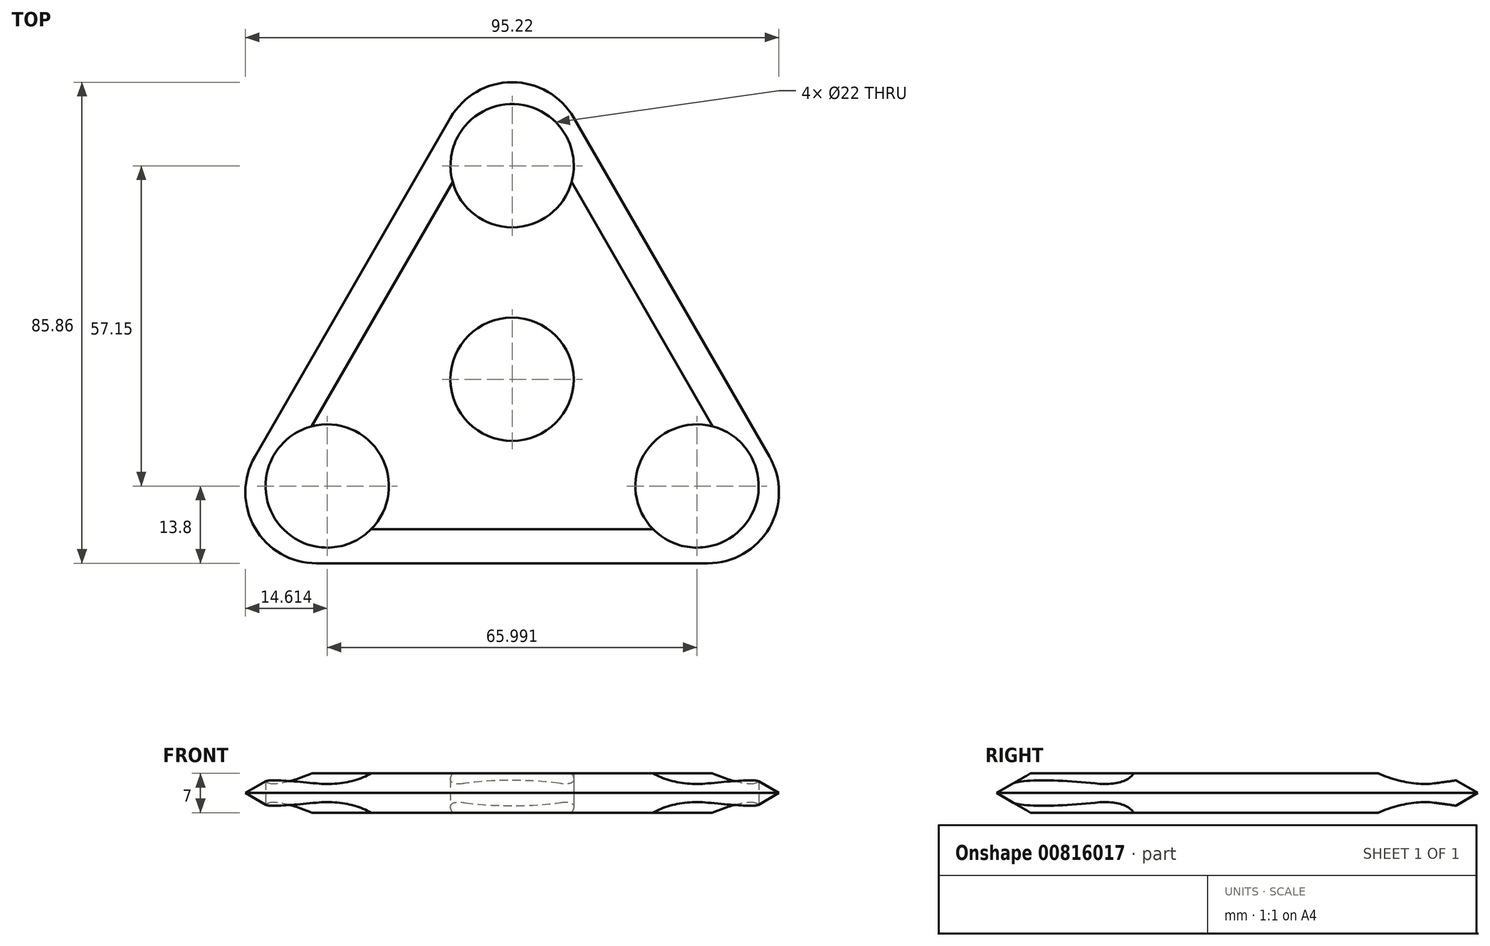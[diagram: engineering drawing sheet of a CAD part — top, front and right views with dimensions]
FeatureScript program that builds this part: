
annotation { "Feature Type Name" : "Feature", "Feature Type Description" : "" }
export const myFeature = defineFeature(function(context is Context, id is Id, definition is map)
    precondition{}
    {
        {
            var Q0;
            Q0=qCreatedBy(makeId("Top.planeOp"),FACE);
            var sketch = newSketch(context, id + "F0", { "sketchPlane" : qUnion([Q0])});
            skCircle(sketch, "E0", {"center": v(0, 0) * mm, "radius": 11 * mm});
            skCircle(sketch, "E1.cCircle", {"center": v(0, 0) * mm, "radius": 19.05 * mm, "construction": true});
            skLineSegment(sketch, "E1.0", {"start": v(0, 38.1) * mm, "end": v(33, -19.05) * mm});
            skLineSegment(sketch, "E1.1", {"start": v(33, -19.05) * mm, "end": v(-33, -19.05) * mm});
            skLineSegment(sketch, "E1.2", {"start": v(-33, -19.05) * mm, "end": v(0, 38.1) * mm});
            skPoint(sketch, "E1.0.midPoint", {"position": v(16.5, 9.53) * mm});
            skCircle(sketch, "E2", {"center": v(0, 38.1) * mm, "radius": 11 * mm});
            skCircle(sketch, "E3.1.0", {"center": v(-33, -19.05) * mm, "radius": 11 * mm});
            skCircle(sketch, "E3.2.0", {"center": v(33, -19.05) * mm, "radius": 11 * mm});
            skLineSegment(sketch, "E4.0", {"start": v(11, 46.66) * mm, "end": v(45.9, -13.8) * mm});
            skLineSegment(sketch, "E4.1", {"start": v(-45.9, -13.8) * mm, "end": v(-11, 46.66) * mm});
            skLineSegment(sketch, "E4.2", {"start": v(34.9, -32.85) * mm, "end": v(-34.9, -32.85) * mm});
            skPoint(sketch, "E5.visualSharp", {"position": v(0, 65.7) * mm});
            skArc(sketch, "E5.filletArc", {"start": v(11, 46.66) * mm, "mid": v(0, 53) * mm, "end": v(-11, 46.66) * mm});
            skPoint(sketch, "E6.visualSharp", {"position": v(-56.9, -32.85) * mm});
            skArc(sketch, "E6.filletArc", {"start": v(-45.9, -13.8) * mm, "mid": v(-45.9, -26.5) * mm, "end": v(-34.9, -32.85) * mm});
            skPoint(sketch, "E7.visualSharp", {"position": v(56.9, -32.85) * mm});
            skArc(sketch, "E7.filletArc", {"start": v(34.9, -32.85) * mm, "mid": v(45.9, -26.5) * mm, "end": v(45.9, -13.8) * mm});
            skSolve(sketch);
        }
        {
            var Q0;
            Q0=makeQuery(id+"F0.imprint","IMPRINT",FACE,{"disambiguationData":[TD([[makeQuery(id+"F0.imprint","IMPRINT",EDGE,{"derivedFrom":sQuery(id+"F0.wireOp",EDGE,"E4.0")}),-1.0]])]});
            var Q1;
            {var subQ0=sQuery(id+"F0.wireOp",EDGE,"E1.2");var subQ1=sQuery(id+"F0.wireOp",EDGE,"E1.0");var subQ2=makeQuery(id+"F0.imprint","INTERSECT",VERTEX,{"derivedFrom":[subQ1,subQ0]});Q1=makeQuery(id+"F0.imprint","IMPRINT",FACE,{"disambiguationData":[TD([[makeQuery(id+"F0.imprint","IMPRINT",EDGE,{"disambiguationData":[TD([[subQ2,-1.0]])],"derivedFrom":subQ1}),1.0]])]});}
            var Q2;
            Q2=makeQuery(id+"F0.imprint","IMPRINT",FACE,{"disambiguationData":[TD([[makeQuery(id+"F0.imprint","IMPRINT",EDGE,{"derivedFrom":sQuery(id+"F0.wireOp",EDGE,"E0")}),-1.0]])]});
            var Q3;
            {var subQ0=sQuery(id+"F0.wireOp",EDGE,"E1.2");var subQ1=sQuery(id+"F0.wireOp",EDGE,"E1.0");var subQ2=makeQuery(id+"F0.imprint","INTERSECT",VERTEX,{"derivedFrom":[subQ1,subQ0]});Q3=makeQuery(id+"F0.imprint","IMPRINT",FACE,{"disambiguationData":[TD([[makeQuery(id+"F0.imprint","IMPRINT",EDGE,{"disambiguationData":[TD([[subQ2,-1.0]])],"derivedFrom":subQ1}),-1.0]])]});}
            var Q4;
            {var subQ0=sQuery(id+"F0.wireOp",EDGE,"E1.2");var subQ1=sQuery(id+"F0.wireOp",EDGE,"E1.1");var subQ2=makeQuery(id+"F0.imprint","INTERSECT",VERTEX,{"derivedFrom":[subQ1,subQ0]});Q4=makeQuery(id+"F0.imprint","IMPRINT",FACE,{"disambiguationData":[TD([[makeQuery(id+"F0.imprint","IMPRINT",EDGE,{"disambiguationData":[TD([[subQ2,1.0]])],"derivedFrom":subQ1}),1.0]])]});}
            var Q5;
            {var subQ0=sQuery(id+"F0.wireOp",EDGE,"E1.1");var subQ1=sQuery(id+"F0.wireOp",EDGE,"E1.0");var subQ2=makeQuery(id+"F0.imprint","INTERSECT",VERTEX,{"derivedFrom":[subQ1,subQ0]});Q5=makeQuery(id+"F0.imprint","IMPRINT",FACE,{"disambiguationData":[TD([[makeQuery(id+"F0.imprint","IMPRINT",EDGE,{"disambiguationData":[TD([[subQ2,1.0]])],"derivedFrom":subQ1}),1.0]])]});}
            var Q6;
            {var subQ0=sQuery(id+"F0.wireOp",EDGE,"E1.1");var subQ1=sQuery(id+"F0.wireOp",EDGE,"E1.0");var subQ2=makeQuery(id+"F0.imprint","INTERSECT",VERTEX,{"derivedFrom":[subQ1,subQ0]});Q6=makeQuery(id+"F0.imprint","IMPRINT",FACE,{"disambiguationData":[TD([[makeQuery(id+"F0.imprint","IMPRINT",EDGE,{"disambiguationData":[TD([[subQ2,1.0]])],"derivedFrom":subQ1}),-1.0]])]});}
            var Q7;
            {var subQ0=sQuery(id+"F0.wireOp",EDGE,"E1.2");var subQ1=sQuery(id+"F0.wireOp",EDGE,"E1.1");var subQ2=makeQuery(id+"F0.imprint","INTERSECT",VERTEX,{"derivedFrom":[subQ1,subQ0]});Q7=makeQuery(id+"F0.imprint","IMPRINT",FACE,{"disambiguationData":[TD([[makeQuery(id+"F0.imprint","IMPRINT",EDGE,{"disambiguationData":[TD([[subQ2,1.0]])],"derivedFrom":subQ1}),-1.0]])]});}
            var Q8;
            Q8=makeQuery(id+"F0.imprint","IMPRINT",FACE,{"disambiguationData":[TD([[makeQuery(id+"F0.imprint","IMPRINT",EDGE,{"derivedFrom":sQuery(id+"F0.wireOp",EDGE,"E0")}),1.0]])]});
            extrude(context, id + "F1", {"entities" : qUnion([Q0, Q1, Q2, Q3, Q4, Q5, Q6, Q7, Q8]), "endBound" : BoundingType.SYMMETRIC, "depth" : 7 * mm, "offsetDistance" : 25.4 * mm, "hasDraft" : true, "draftAngle" : 60 * degree, "draftPullDirection" : true});
        }
        {
            var Q0;
            {var subQ0=sQuery(id+"F0.wireOp",EDGE,"E1.2");var subQ1=sQuery(id+"F0.wireOp",EDGE,"E1.1");var subQ2=makeQuery(id+"F0.imprint","INTERSECT",VERTEX,{"derivedFrom":[subQ1,subQ0]});Q0=makeQuery(id+"F0.imprint","IMPRINT",FACE,{"disambiguationData":[TD([[makeQuery(id+"F0.imprint","IMPRINT",EDGE,{"disambiguationData":[TD([[subQ2,1.0]])],"derivedFrom":subQ1}),1.0]])]});}
            var Q1;
            {var subQ0=sQuery(id+"F0.wireOp",EDGE,"E1.2");var subQ1=sQuery(id+"F0.wireOp",EDGE,"E1.1");var subQ2=makeQuery(id+"F0.imprint","INTERSECT",VERTEX,{"derivedFrom":[subQ1,subQ0]});Q1=makeQuery(id+"F0.imprint","IMPRINT",FACE,{"disambiguationData":[TD([[makeQuery(id+"F0.imprint","IMPRINT",EDGE,{"disambiguationData":[TD([[subQ2,1.0]])],"derivedFrom":subQ1}),-1.0]])]});}
            var Q2;
            Q2=makeQuery(id+"F0.imprint","IMPRINT",FACE,{"disambiguationData":[TD([[makeQuery(id+"F0.imprint","IMPRINT",EDGE,{"derivedFrom":sQuery(id+"F0.wireOp",EDGE,"E0")}),1.0]])]});
            var Q3;
            {var subQ0=sQuery(id+"F0.wireOp",EDGE,"E1.2");var subQ1=sQuery(id+"F0.wireOp",EDGE,"E1.0");var subQ2=makeQuery(id+"F0.imprint","INTERSECT",VERTEX,{"derivedFrom":[subQ1,subQ0]});Q3=makeQuery(id+"F0.imprint","IMPRINT",FACE,{"disambiguationData":[TD([[makeQuery(id+"F0.imprint","IMPRINT",EDGE,{"disambiguationData":[TD([[subQ2,-1.0]])],"derivedFrom":subQ1}),1.0]])]});}
            var Q4;
            {var subQ0=sQuery(id+"F0.wireOp",EDGE,"E1.2");var subQ1=sQuery(id+"F0.wireOp",EDGE,"E1.0");var subQ2=makeQuery(id+"F0.imprint","INTERSECT",VERTEX,{"derivedFrom":[subQ1,subQ0]});Q4=makeQuery(id+"F0.imprint","IMPRINT",FACE,{"disambiguationData":[TD([[makeQuery(id+"F0.imprint","IMPRINT",EDGE,{"disambiguationData":[TD([[subQ2,-1.0]])],"derivedFrom":subQ1}),-1.0]])]});}
            var Q5;
            {var subQ0=sQuery(id+"F0.wireOp",EDGE,"E1.1");var subQ1=sQuery(id+"F0.wireOp",EDGE,"E1.0");var subQ2=makeQuery(id+"F0.imprint","INTERSECT",VERTEX,{"derivedFrom":[subQ1,subQ0]});Q5=makeQuery(id+"F0.imprint","IMPRINT",FACE,{"disambiguationData":[TD([[makeQuery(id+"F0.imprint","IMPRINT",EDGE,{"disambiguationData":[TD([[subQ2,1.0]])],"derivedFrom":subQ1}),-1.0]])]});}
            var Q6;
            {var subQ0=sQuery(id+"F0.wireOp",EDGE,"E1.1");var subQ1=sQuery(id+"F0.wireOp",EDGE,"E1.0");var subQ2=makeQuery(id+"F0.imprint","INTERSECT",VERTEX,{"derivedFrom":[subQ1,subQ0]});Q6=makeQuery(id+"F0.imprint","IMPRINT",FACE,{"disambiguationData":[TD([[makeQuery(id+"F0.imprint","IMPRINT",EDGE,{"disambiguationData":[TD([[subQ2,1.0]])],"derivedFrom":subQ1}),1.0]])]});}
            extrude(context, id + "F2", {"entities" : qUnion([Q0, Q1, Q2, Q3, Q4, Q5, Q6]), "operationType" : NewBodyOperationType.REMOVE, "endBound" : BoundingType.SYMMETRIC, "depth" : 25.4 * mm, "offsetDistance" : 25.4 * mm});
        }
    });
